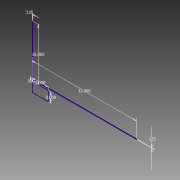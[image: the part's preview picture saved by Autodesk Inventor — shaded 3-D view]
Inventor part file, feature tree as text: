
AUTODESK INVENTOR PART (.ipt)
format: ipt  version: 2013 (Build 170138000, 138)  size: 66,048 bytes
history: native  units: in
note: dims shown in document units (in); Inventor stores cm internally (conversion verified against a paired STEP export)
features: sketch x1
ambient origin geometry x8: Origin, YZ Plane, XZ Plane, XY Plane, X Axis, Y Axis, Z Axis, Center Point
feature tree (1):
  sketch  "Sketch1"  dims[d0=5.0in d1=3.0in d2=0.125in d3=16.0in d4=0.5in d5=32.0in d6=0.125in]
